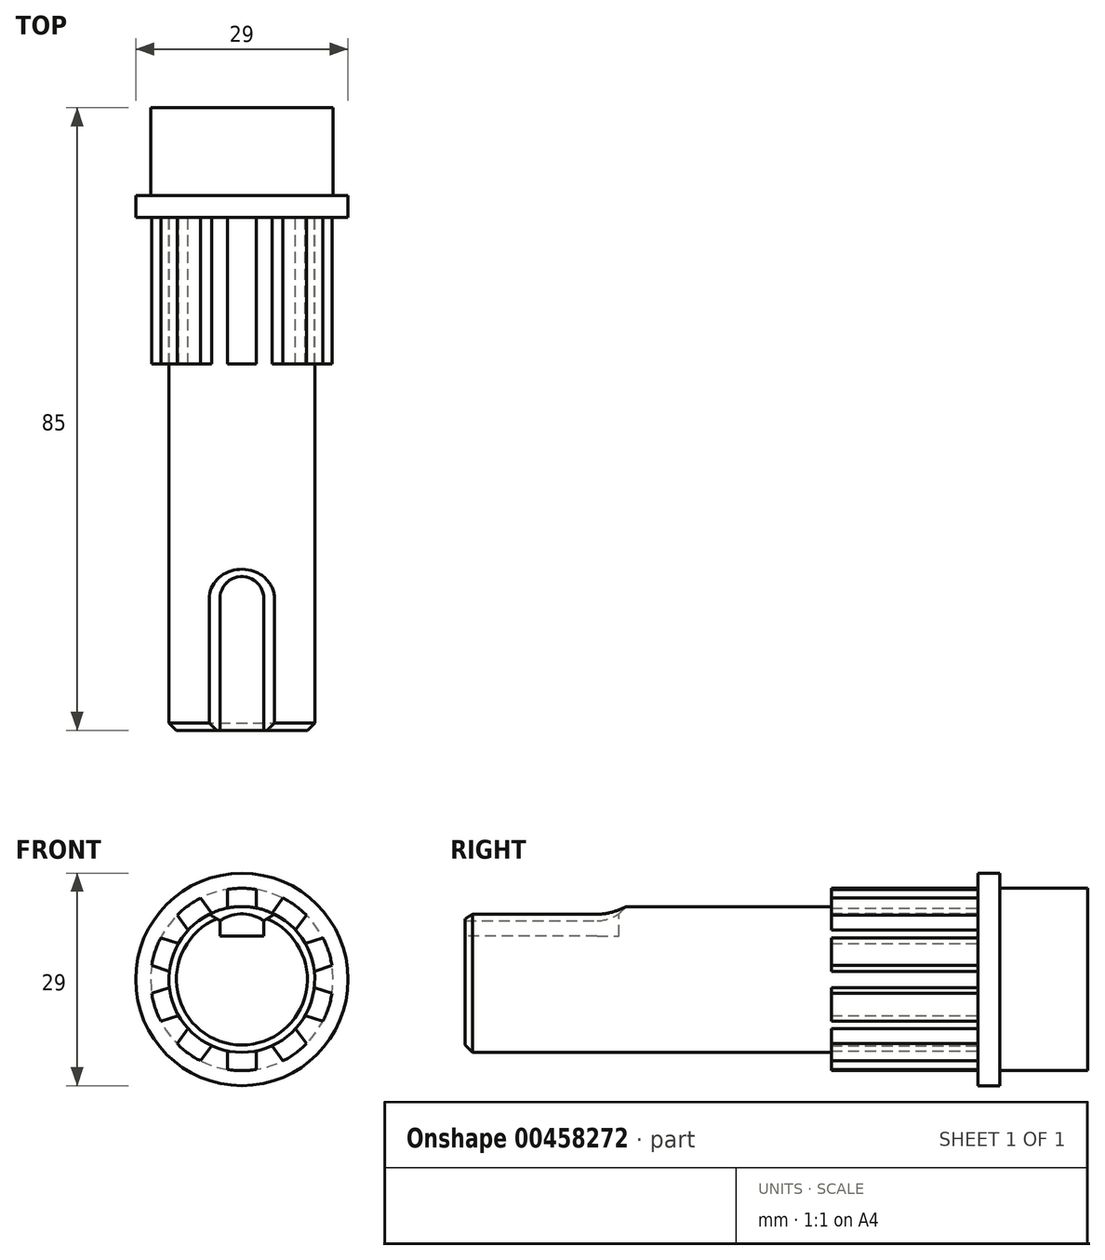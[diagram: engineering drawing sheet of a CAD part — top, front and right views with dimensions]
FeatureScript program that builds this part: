
annotation { "Feature Type Name" : "Feature", "Feature Type Description" : "" }
export const myFeature = defineFeature(function(context is Context, id is Id, definition is map)
    precondition{}
    {
        {
            var Q0;
            Q0=qCreatedBy(makeId("Front.planeOp"),FACE);
            var sketch = newSketch(context, id + "F0", { "sketchPlane" : qUnion([Q0])});
            skCircle(sketch, "E0", {"center": v(0, 0) * mm, "radius": 12.45 * mm});
            skSolve(sketch);
        }
        {
            var Q0;
            Q0 = qSketchRegion(id + "F0", true);
            extrude(context, id + "F1", {"entities" : qUnion([Q0]), "depth" : -12 * mm});
        }
        {
            var Q0;
            Q0=qCreatedBy(makeId("Front.planeOp"),FACE);
            var sketch = newSketch(context, id + "F2", { "sketchPlane" : qUnion([Q0])});
            skCircle(sketch, "E1", {"center": v(0, 0) * mm, "radius": 14.5 * mm});
            skSolve(sketch);
        }
        {
            var Q0;
            Q0 = qSketchRegion(id + "F2", true);
            extrude(context, id + "F3", {"entities" : qUnion([Q0]), "operationType" : NewBodyOperationType.ADD, "depth" : 3 * mm});
        }
        {
            var Q0;
            Q0=makeQuery(id+"F3.opExtrude","CAP_FACE",FACE,{"disambiguationData":[OSD([sQuery(id+"F2.wireOp",EDGE,"E1")])],"isStart":false});
            var sketch = newSketch(context, id + "F4", { "sketchPlane" : qUnion([Q0])});
            skCircle(sketch, "E2", {"center": v(0, 0) * mm, "radius": 9.95 * mm});
            skSolve(sketch);
        }
        {
            var Q0;
            Q0 = qSketchRegion(id + "F4", true);
            extrude(context, id + "F5", {"entities" : qUnion([Q0]), "operationType" : NewBodyOperationType.ADD, "depth" : 70 * mm});
        }
        {
            var Q0;
            Q0=qCreatedBy(makeId("Front.planeOp"),FACE);
            cPlane(context, id + "F6", {"entities" : qUnion([Q0]), "cplaneType" : CPlaneType.OFFSET, "offset" : 3 * mm, "width" : 150 * mm, "height" : 150 * mm});
        }
        {
            var Q0;
            Q0=qCreatedBy(id+"F6.planeOp",FACE);
            var sketch = newSketch(context, id + "F7", { "sketchPlane" : qUnion([Q0])});
            skCircle(sketch, "E3", {"center": v(0, 0) * mm, "radius": 9.95 * mm});
            skArc(sketch, "E4", {"start": v(1.99, 12.29) * mm, "mid": v(0, 12.45) * mm, "end": v(-1.99, 12.29) * mm});
            skLineSegment(sketch, "E5", {"start": v(-1.99, 9.75) * mm, "end": v(-1.99, 12.29) * mm});
            skLineSegment(sketch, "E6", {"start": v(1.99, 9.75) * mm, "end": v(1.99, 12.29) * mm});
            skPoint(sketch, "E7.center.orphan", {"position": v(0, 9.95) * mm});
            skArc(sketch, "E8.1.0", {"start": v(-5.61, 11.11) * mm, "mid": v(-7.32, 10.07) * mm, "end": v(-8.83, 8.77) * mm});
            skLineSegment(sketch, "E8.1.1", {"start": v(-7.34, 6.72) * mm, "end": v(-8.83, 8.77) * mm});
            skLineSegment(sketch, "E8.1.2", {"start": v(-4.12, 9.06) * mm, "end": v(-5.61, 11.11) * mm});
            skArc(sketch, "E8.2.0", {"start": v(-11.07, 5.7) * mm, "mid": v(-11.84, 3.85) * mm, "end": v(-12.3, 1.9) * mm});
            skLineSegment(sketch, "E8.2.1", {"start": v(-9.89, 1.12) * mm, "end": v(-12.3, 1.9) * mm});
            skLineSegment(sketch, "E8.2.2", {"start": v(-8.66, 4.9) * mm, "end": v(-11.07, 5.7) * mm});
            skArc(sketch, "E8.3.0", {"start": v(-12.3, -1.9) * mm, "mid": v(-11.84, -3.85) * mm, "end": v(-11.07, -5.7) * mm});
            skLineSegment(sketch, "E8.3.1", {"start": v(-8.66, -4.9) * mm, "end": v(-11.07, -5.7) * mm});
            skLineSegment(sketch, "E8.3.2", {"start": v(-9.89, -1.12) * mm, "end": v(-12.3, -1.9) * mm});
            skArc(sketch, "E8.4.0", {"start": v(-8.83, -8.77) * mm, "mid": v(-7.32, -10.07) * mm, "end": v(-5.61, -11.11) * mm});
            skLineSegment(sketch, "E8.4.1", {"start": v(-4.12, -9.06) * mm, "end": v(-5.61, -11.11) * mm});
            skLineSegment(sketch, "E8.4.2", {"start": v(-7.34, -6.72) * mm, "end": v(-8.83, -8.77) * mm});
            skArc(sketch, "E8.5.0", {"start": v(-1.99, -12.29) * mm, "mid": v(0, -12.45) * mm, "end": v(1.99, -12.29) * mm});
            skLineSegment(sketch, "E8.5.1", {"start": v(1.99, -9.75) * mm, "end": v(1.99, -12.29) * mm});
            skLineSegment(sketch, "E8.5.2", {"start": v(-1.99, -9.75) * mm, "end": v(-1.99, -12.29) * mm});
            skArc(sketch, "E8.6.0", {"start": v(5.61, -11.11) * mm, "mid": v(7.32, -10.07) * mm, "end": v(8.83, -8.77) * mm});
            skLineSegment(sketch, "E8.6.1", {"start": v(7.34, -6.72) * mm, "end": v(8.83, -8.77) * mm});
            skLineSegment(sketch, "E8.6.2", {"start": v(4.12, -9.06) * mm, "end": v(5.61, -11.11) * mm});
            skArc(sketch, "E8.7.0", {"start": v(11.07, -5.7) * mm, "mid": v(11.84, -3.85) * mm, "end": v(12.3, -1.9) * mm});
            skLineSegment(sketch, "E8.7.1", {"start": v(9.89, -1.12) * mm, "end": v(12.3, -1.9) * mm});
            skLineSegment(sketch, "E8.7.2", {"start": v(8.66, -4.9) * mm, "end": v(11.07, -5.7) * mm});
            skArc(sketch, "E8.8.0", {"start": v(12.3, 1.9) * mm, "mid": v(11.84, 3.85) * mm, "end": v(11.07, 5.7) * mm});
            skLineSegment(sketch, "E8.8.1", {"start": v(8.66, 4.9) * mm, "end": v(11.07, 5.7) * mm});
            skLineSegment(sketch, "E8.8.2", {"start": v(9.89, 1.12) * mm, "end": v(12.3, 1.9) * mm});
            skArc(sketch, "E8.9.0", {"start": v(8.83, 8.77) * mm, "mid": v(7.32, 10.07) * mm, "end": v(5.61, 11.11) * mm});
            skLineSegment(sketch, "E8.9.1", {"start": v(4.12, 9.06) * mm, "end": v(5.61, 11.11) * mm});
            skLineSegment(sketch, "E8.9.2", {"start": v(7.34, 6.72) * mm, "end": v(8.83, 8.77) * mm});
            skSolve(sketch);
        }
        {
            var Q0;
            Q0 = qSketchRegion(id + "F7", true);
            extrude(context, id + "F8", {"entities" : qUnion([Q0]), "operationType" : NewBodyOperationType.ADD, "depth" : 20 * mm, "offsetDistance" : 25 * mm});
        }
        {
            var Q0;
            Q0=qCreatedBy(makeId("Top.planeOp"),FACE);
            cPlane(context, id + "F9", {"entities" : qUnion([Q0]), "cplaneType" : CPlaneType.OFFSET, "offset" : 9.95 * mm, "width" : 150 * mm, "height" : 150 * mm});
        }
        {
            var Q0;
            Q0=qCreatedBy(id+"F9.planeOp",FACE);
            var sketch = newSketch(context, id + "F10", { "sketchPlane" : qUnion([Q0])});
            skArc(sketch, "E9", {"start": v(3, -55) * mm, "mid": v(0, -52) * mm, "end": v(-3, -55) * mm});
            skLineSegment(sketch, "E10", {"start": v(3, -55) * mm, "end": v(3, -73) * mm});
            skLineSegment(sketch, "E11", {"start": v(-3, -73) * mm, "end": v(-3, -55) * mm});
            skLineSegment(sketch, "E12", {"start": v(-3, -73) * mm, "end": v(3, -73) * mm});
            skSolve(sketch);
        }
        {
            var Q0;
            Q0 = qSketchRegion(id + "F10", true);
            extrude(context, id + "F11", {"entities" : qUnion([Q0]), "operationType" : NewBodyOperationType.REMOVE, "oppositeDirection" : true, "depth" : 4 * mm, "offsetDistance" : 25 * mm});
        }
        {
            var Q0;
            Q0=makeQuery(id+"F11.boolean.opBoolean","INTERSECT",EDGE,{"derivedFrom":[makeQuery(id+"F5.opExtrude","SWEPT_FACE",FACE,{"disambiguationData":[OSD([sQuery(id+"F4.wireOp",EDGE,"E2")])]}),makeQuery(id+"F11.opExtrude","SWEPT_FACE",FACE,{"disambiguationData":[OSD([sQuery(id+"F10.wireOp",EDGE,"E11")])]})]});
            var Q1;
            Q1=makeQuery(id+"F11.boolean.opBoolean","INTERSECT",EDGE,{"derivedFrom":[makeQuery(id+"F5.opExtrude","SWEPT_FACE",FACE,{"disambiguationData":[OSD([sQuery(id+"F4.wireOp",EDGE,"E2")])]}),makeQuery(id+"F11.opExtrude","SWEPT_FACE",FACE,{"disambiguationData":[OSD([sQuery(id+"F10.wireOp",EDGE,"E9")])]})]});
            var Q2;
            Q2=makeQuery(id+"F11.boolean.opBoolean","INTERSECT",EDGE,{"derivedFrom":[makeQuery(id+"F5.opExtrude","SWEPT_FACE",FACE,{"disambiguationData":[OSD([sQuery(id+"F4.wireOp",EDGE,"E2")])]}),makeQuery(id+"F11.opExtrude","SWEPT_FACE",FACE,{"disambiguationData":[OSD([sQuery(id+"F10.wireOp",EDGE,"E10")])]})]});
            var Q3;
            Q3=makeQuery(id+"F5.opExtrude","CAP_EDGE",EDGE,{"disambiguationData":[OSD([sQuery(id+"F4.wireOp",EDGE,"E2")])],"isStart":false});
            chamfer(context, id + "F12", {"entities" : qUnion([Q0, Q1, Q2, Q3]), "width" : 1 * mm, "tangentPropagation" : true});
        }
    });
